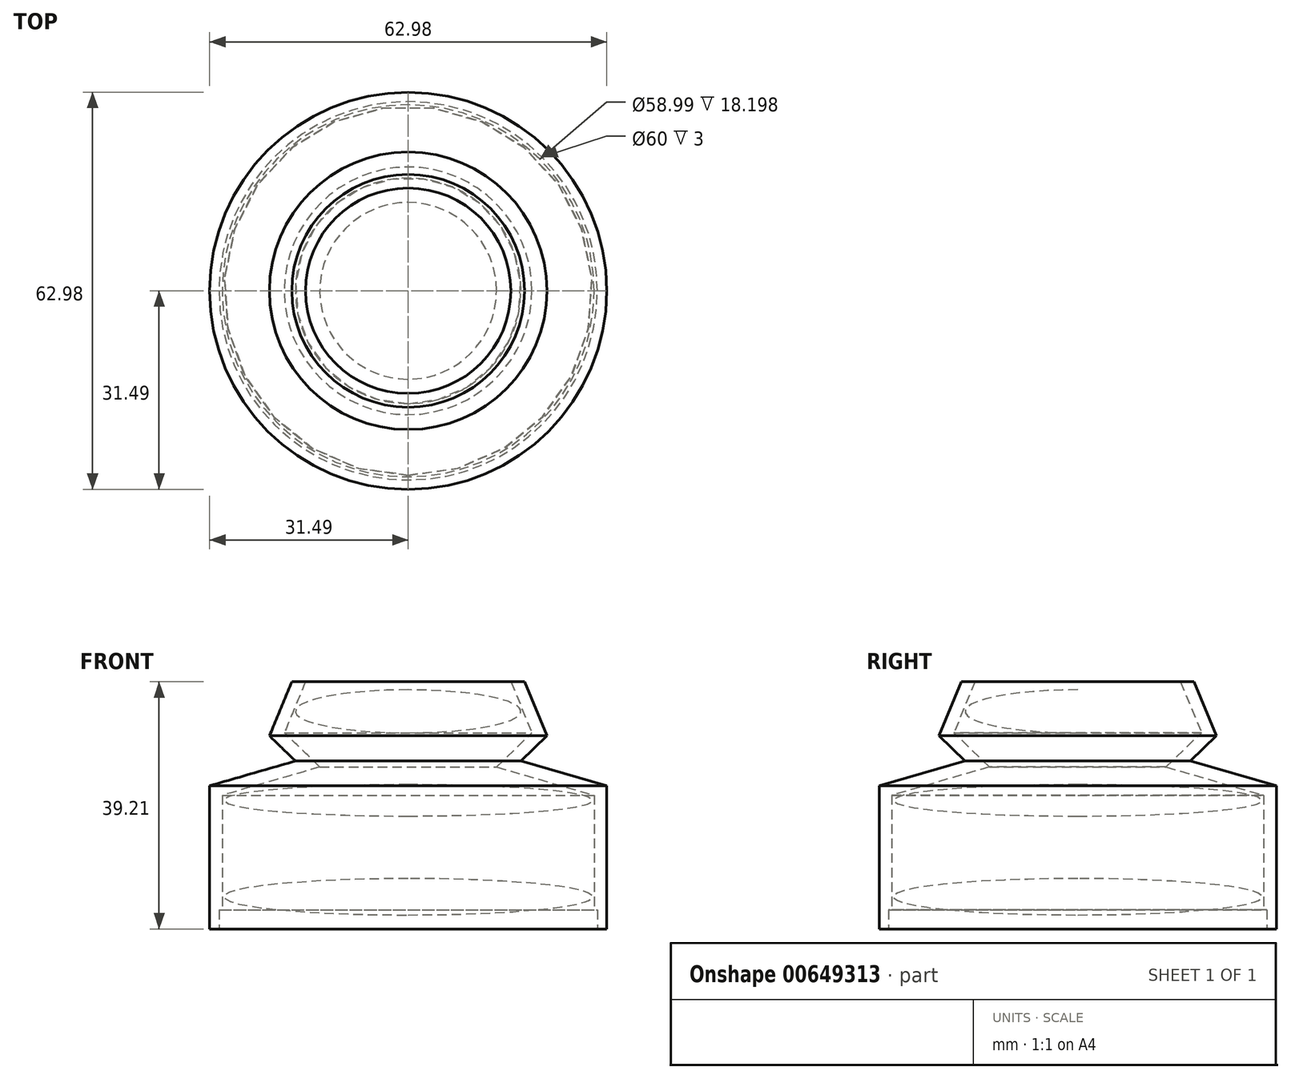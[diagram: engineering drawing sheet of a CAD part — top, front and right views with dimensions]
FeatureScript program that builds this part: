
annotation { "Feature Type Name" : "Feature", "Feature Type Description" : "" }
export const myFeature = defineFeature(function(context is Context, id is Id, definition is map)
    precondition{}
    {
        {
            var Q0;
            Q0=qCreatedBy(makeId("Right.planeOp"),FACE);
            var sketch = newSketch(context, id + "F0", { "sketchPlane" : qUnion([Q0])});
            skLineSegment(sketch, "E0", {"start": v(0, 0) * mm, "end": v(0, 98.08) * mm});
            skSolve(sketch);
        }
        {
            var Q0;
            Q0=qCreatedBy(makeId("Front.planeOp"),FACE);
            var sketch = newSketch(context, id + "F1", { "sketchPlane" : qUnion([Q0])});
            skLineSegment(sketch, "E1", {"start": v(0, 0) * mm, "end": v(-31.5, 0) * mm});
            skLineSegment(sketch, "E2", {"start": v(-31.5, 0) * mm, "end": v(-31.5, 22.7) * mm});
            skLineSegment(sketch, "E3", {"start": v(-31.5, 22.7) * mm, "end": v(-17.89, 26.64) * mm});
            skLineSegment(sketch, "E4", {"start": v(-17.89, 26.64) * mm, "end": v(-22, 30.62) * mm});
            skLineSegment(sketch, "E5", {"start": v(-22, 30.62) * mm, "end": v(-18.45, 39.2) * mm});
            skLineSegment(sketch, "E6", {"start": v(-18.45, 39.2) * mm, "end": v(0, 39.2) * mm});
            skLineSegment(sketch, "E7", {"start": v(0, 39.2) * mm, "end": v(0, 0) * mm});
            skSolve(sketch);
        }
        {
            var Q0;
            Q0=makeQuery(id+"F1.imprint","IMPRINT",FACE,{"disambiguationData":[TD([[makeQuery(id+"F1.imprint","IMPRINT",EDGE,{"derivedFrom":sQuery(id+"F1.wireOp",EDGE,"E1")}),-1.0]])]});
            var Q1;
            Q1=sQuery(id+"F0.wireOp",EDGE,"E0");
            revolve(context, id + "F2", {"entities" : qUnion([Q0]), "axis" : qUnion([Q1]), "revolveType" : RevolveType.FULL});
        }
        {
            var Q0;
            Q0=makeQuery(id+"F2.opRevolve","SWEPT_FACE",FACE,{"disambiguationData":[OSD([sQuery(id+"F1.wireOp",EDGE,"E6")])]});
            shell(context, id + "F3", {"entities" : qUnion([Q0]), "thickness" : 2 * mm});
        }
        {
            var Q0;
            Q0=makeQuery(id+"F2.opRevolve","SWEPT_FACE",FACE,{"disambiguationData":[OSD([sQuery(id+"F1.wireOp",EDGE,"E1")])]});
            var sketch = newSketch(context, id + "F4", { "sketchPlane" : qUnion([Q0])});
            skCircle(sketch, "E8", {"center": v(0, 0) * mm, "radius": 30 * mm});
            skSolve(sketch);
        }
        {
            var Q0;
            Q0=makeQuery(id+"F4.imprint","IMPRINT",FACE,{"disambiguationData":[TD([[makeQuery(id+"F4.imprint","IMPRINT",EDGE,{"derivedFrom":sQuery(id+"F4.wireOp",EDGE,"E8")}),1.0]])]});
            extrude(context, id + "F5", {"entities" : qUnion([Q0]), "operationType" : NewBodyOperationType.REMOVE, "oppositeDirection" : true, "depth" : 3 * mm, "offsetDistance" : 25 * mm});
        }
        {
            var Q0;
            Q0=qCreatedBy(makeId("Right.planeOp"),FACE);
            var sketch = newSketch(context, id + "F6", { "sketchPlane" : qUnion([Q0])});
            skEllipticalArc(sketch, "E9", {});
            skEllipticalArc(sketch, "E10", {});
            skEllipticalArc(sketch, "E11", {});
            skPoint(sketch, "E12.orphan", {"position": v(0, -3) * mm});
            skLineSegment(sketch, "E13.trimOffspring", {"start": v(0, 7.99) * mm, "end": v(0, 2.22) * mm});
            skLineSegment(sketch, "E14.trimOffspring", {"start": v(0, 22.89) * mm, "end": v(0, 17.9) * mm});
            skLineSegment(sketch, "E15", {"start": v(0, 31.1) * mm, "end": v(0, 37.92) * mm});
            const initialGuessF6  = {"E9": [0, 0.034508105367422104, 1, 0, 0.01788613200187683, 0.0034116004958613696, 1.5707963267948966, 4.71238898038469], "E10": [0, 0.005102757830172777, 1, 0, 0.029251746833324432, 0.0028851976366458354, 1.5707963267948966, 4.71238898038469], "E11": [0, 0.020389800891280174, 1, 0, 0.02919512800872326, 0.002495977428633082, 1.5707963267948966, 4.71238898038469]};
            skSetInitialGuess(sketch, initialGuessF6);
            skSolve(sketch);
        }
        {
            var Q0;
            Q0=makeQuery(id+"F6.imprint","IMPRINT",FACE,{"disambiguationData":[TD([[makeQuery(id+"F6.imprint","IMPRINT",EDGE,{"derivedFrom":sQuery(id+"F6.wireOp",EDGE,"E9")}),1.0]])]});
            var Q1;
            Q1=makeQuery(id+"F6.imprint","IMPRINT",FACE,{"disambiguationData":[TD([[makeQuery(id+"F6.imprint","IMPRINT",EDGE,{"derivedFrom":sQuery(id+"F6.wireOp",EDGE,"E11")}),1.0]])]});
            var Q2;
            Q2=makeQuery(id+"F6.imprint","IMPRINT",FACE,{"disambiguationData":[TD([[makeQuery(id+"F6.imprint","IMPRINT",EDGE,{"derivedFrom":sQuery(id+"F6.wireOp",EDGE,"E10")}),1.0]])]});
            var Q3;
            Q3=sQuery(id+"F0.wireOp",EDGE,"E0");
            revolve(context, id + "F7", {"entities" : qUnion([Q0, Q1, Q2]), "axis" : qUnion([Q3]), "revolveType" : RevolveType.FULL});
        }
    });
